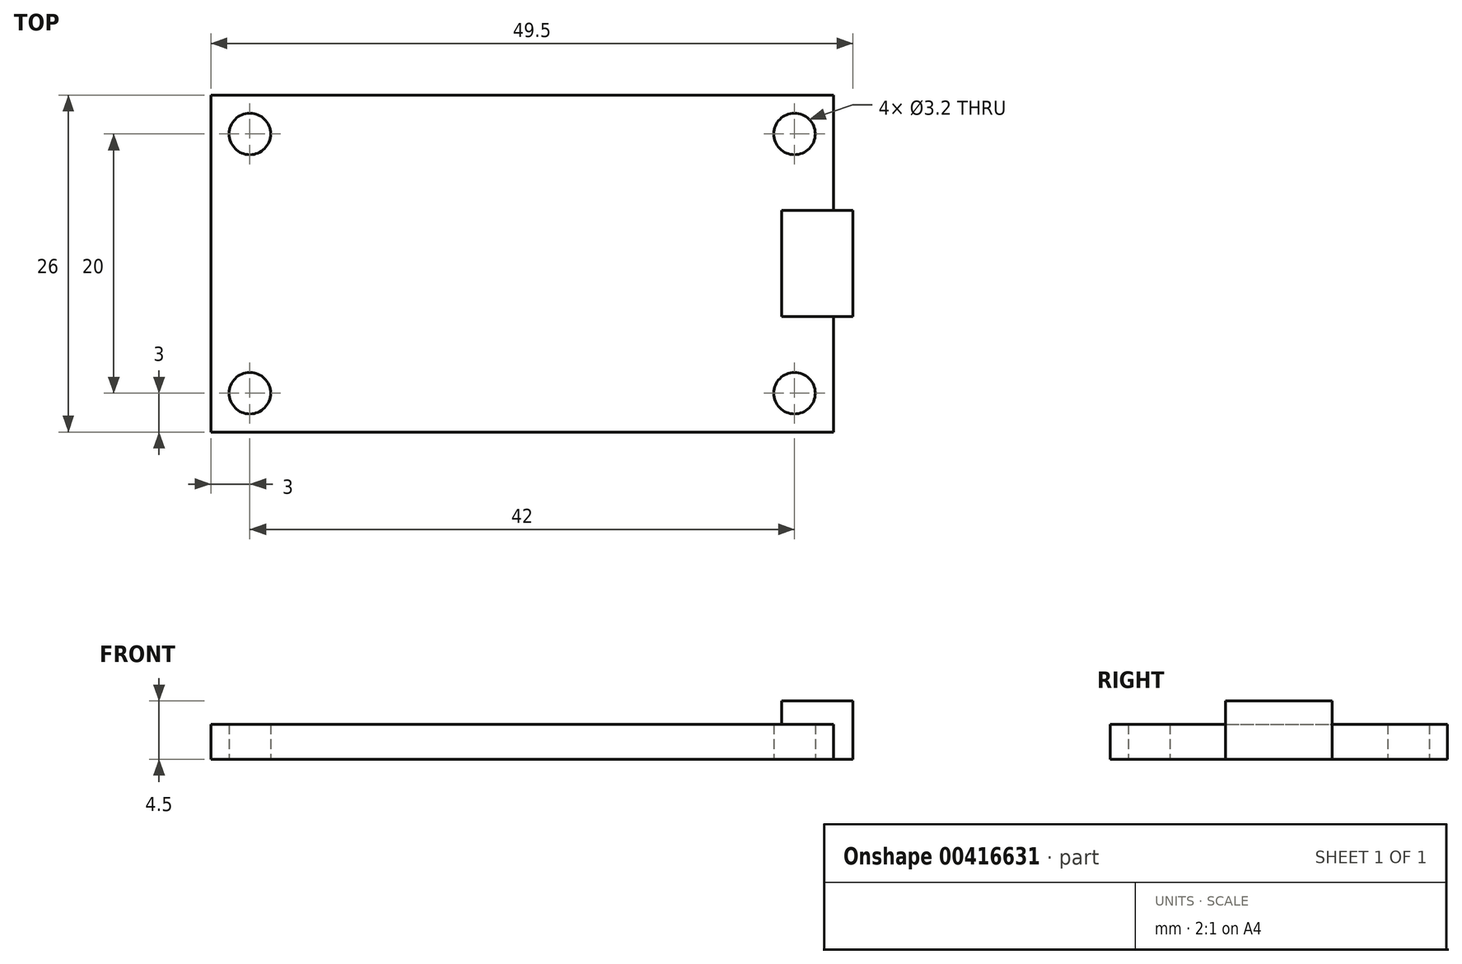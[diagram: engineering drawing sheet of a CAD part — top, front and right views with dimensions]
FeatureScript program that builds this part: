
annotation { "Feature Type Name" : "Feature", "Feature Type Description" : "" }
export const myFeature = defineFeature(function(context is Context, id is Id, definition is map)
    precondition{}
    {
        {
            var Q0;
            Q0=qCreatedBy(makeId("Top.planeOp"),FACE);
            var sketch = newSketch(context, id + "F0", { "sketchPlane" : qUnion([Q0])});
            skLineSegment(sketch, "E0.bottom", {"start": v(-24, -13) * mm, "end": v(24, -13) * mm});
            skLineSegment(sketch, "E0.top", {"start": v(-24, 13) * mm, "end": v(24, 13) * mm});
            skLineSegment(sketch, "E0.left", {"start": v(-24, -13) * mm, "end": v(-24, 13) * mm});
            skLineSegment(sketch, "E0.right", {"start": v(24, -13) * mm, "end": v(24, 13) * mm});
            skPoint(sketch, "E0.middle", {"position": v(0, 0) * mm});
            skCircle(sketch, "E1", {"center": v(-21, 10) * mm, "radius": 1.6 * mm});
            skCircle(sketch, "E2", {"center": v(21, 10) * mm, "radius": 1.6 * mm});
            skCircle(sketch, "E3", {"center": v(-21, -10) * mm, "radius": 1.6 * mm});
            skCircle(sketch, "E4", {"center": v(21, -10) * mm, "radius": 1.6 * mm});
            skLineSegment(sketch, "E5.bottom", {"start": v(25.5, 4.1) * mm, "end": v(20, 4.1) * mm});
            skLineSegment(sketch, "E5.top", {"start": v(25.5, -4.1) * mm, "end": v(20, -4.1) * mm});
            skLineSegment(sketch, "E5.left", {"start": v(25.5, 4.1) * mm, "end": v(25.5, -4.1) * mm});
            skLineSegment(sketch, "E5.right", {"start": v(20, 4.1) * mm, "end": v(20, -4.1) * mm});
            skPoint(sketch, "E5.middle", {"position": v(22.75, 0) * mm});
            skPoint(sketch, "E5.middle.positionSnap0", {"position": v(24, 0) * mm});
            skPoint(sketch, "E5.centerSnap0", {"position": v(24, 0) * mm});
            skLineSegment(sketch, "E6.bottom", {"start": v(-24, 8) * mm, "end": v(1, 8) * mm});
            skLineSegment(sketch, "E6.top", {"start": v(-24, -8) * mm, "end": v(1, -8) * mm});
            skLineSegment(sketch, "E6.left", {"start": v(-24, 8) * mm, "end": v(-24, -8) * mm});
            skLineSegment(sketch, "E6.right", {"start": v(1, 8) * mm, "end": v(1, -8) * mm});
            skPoint(sketch, "E6.middle", {"position": v(-11.5, 0) * mm});
            skLineSegment(sketch, "E7.bottom", {"start": v(-24, 13) * mm, "end": v(14, 13) * mm});
            skLineSegment(sketch, "E7.top", {"start": v(-24, 10.3) * mm, "end": v(14, 10.3) * mm});
            skLineSegment(sketch, "E7.left", {"start": v(-24, 13) * mm, "end": v(-24, 10.3) * mm});
            skLineSegment(sketch, "E7.right", {"start": v(14, 13) * mm, "end": v(14, 10.3) * mm});
            skLineSegment(sketch, "E8.bottom", {"start": v(-24, -13) * mm, "end": v(14, -13) * mm});
            skLineSegment(sketch, "E8.top", {"start": v(-24, -10.3) * mm, "end": v(14, -10.3) * mm});
            skLineSegment(sketch, "E8.left", {"start": v(-24, -13) * mm, "end": v(-24, -10.3) * mm});
            skLineSegment(sketch, "E8.right", {"start": v(14, -13) * mm, "end": v(14, -10.3) * mm});
            skSolve(sketch);
        }
        {
            var Q0;
            Q0=qSketchRegion(id+"F0",true);
            extrude(context, id + "F1", {"entities" : qUnion([Q0]), "depth" : 2.7 * mm});
        }
        {
            var Q0;
            {var subQ5=sQuery(id+"F0.wireOp",EDGE,"E5.right");Q0=makeQuery(id+"F0.imprint","IMPRINT",FACE,{"disambiguationData":[TD([[makeQuery(id+"F0.imprint","IMPRINT",EDGE,{"derivedFrom":subQ5}),1.0]])]});}
            var Q1;
            {var subQ5=sQuery(id+"F0.wireOp",EDGE,"E5.left");Q1=makeQuery(id+"F0.imprint","IMPRINT",FACE,{"disambiguationData":[TD([[makeQuery(id+"F0.imprint","IMPRINT",EDGE,{"derivedFrom":subQ5}),-1.0]])]});}
            extrude(context, id + "F2", {"entities" : qUnion([Q0, Q1]), "operationType" : NewBodyOperationType.ADD, "depth" : 4.5 * mm});
        }
    });
